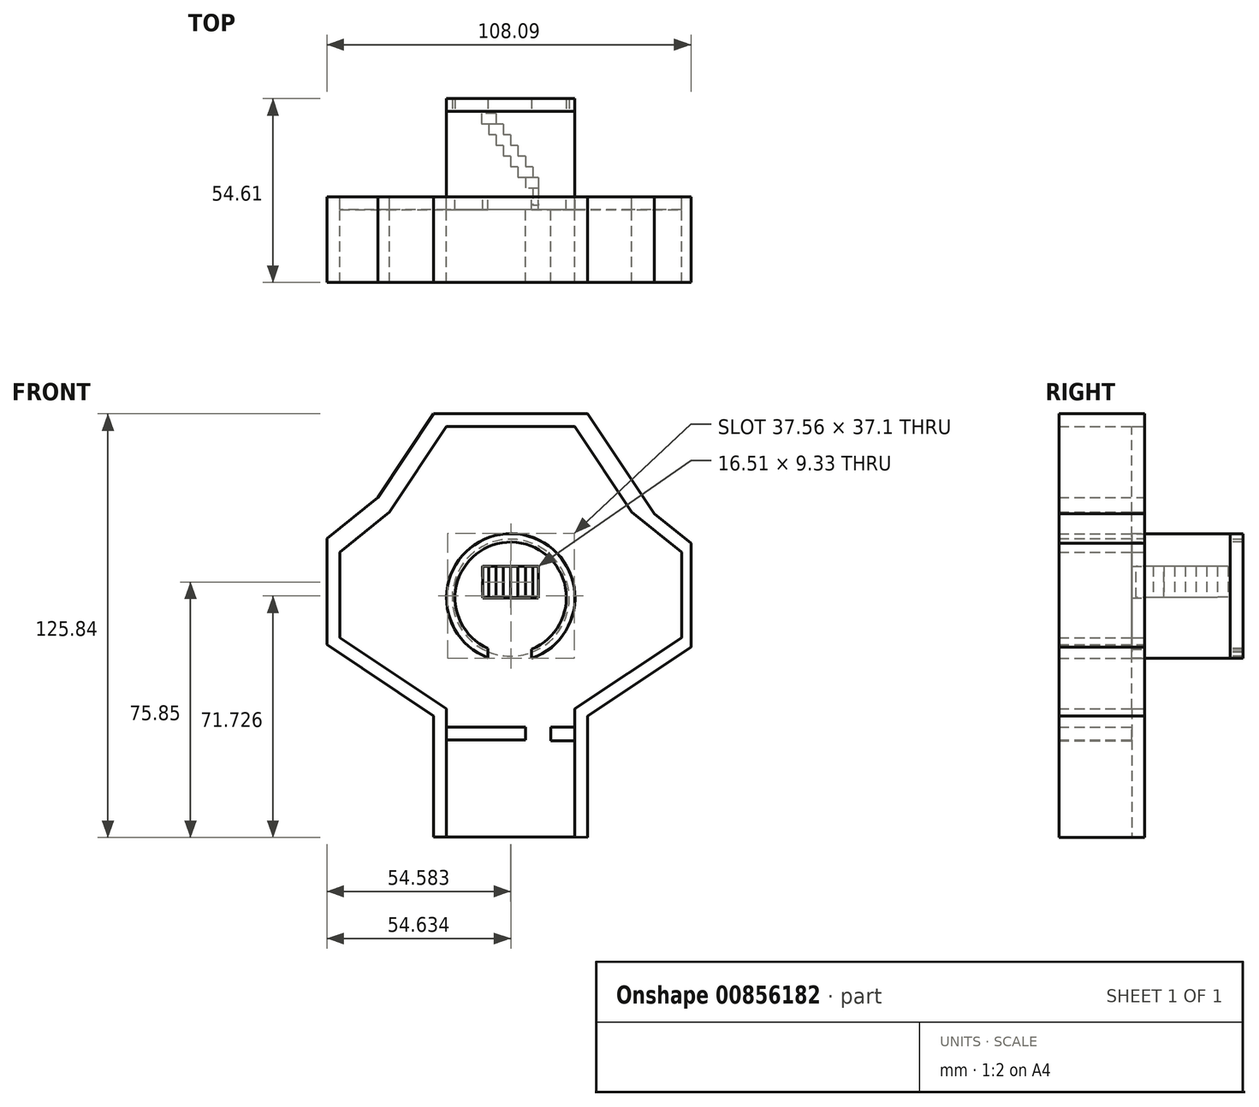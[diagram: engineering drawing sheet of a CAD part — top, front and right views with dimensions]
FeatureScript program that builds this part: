
annotation { "Feature Type Name" : "Feature", "Feature Type Description" : "" }
export const myFeature = defineFeature(function(context is Context, id is Id, definition is map)
    precondition{}
    {
        {
            var Q0;
            Q0=qCreatedBy(makeId("Front.planeOp"),FACE);
            var sketch = newSketch(context, id + "F0", { "sketchPlane" : qUnion([Q0])});
            skLineSegment(sketch, "E0.left", {"start": v(-51.03, 0) * mm, "end": v(-51.03, -38.1) * mm});
            skLineSegment(sketch, "E0.right", {"start": v(-12.93, 0) * mm, "end": v(-12.93, -38.1) * mm});
            skLineSegment(sketch, "E1", {"start": v(-12.93, 0) * mm, "end": v(18.8, 21.1) * mm});
            skLineSegment(sketch, "E2", {"start": v(18.8, 21.1) * mm, "end": v(18.8, 46.5) * mm});
            skLineSegment(sketch, "E3", {"start": v(18.8, 46.5) * mm, "end": v(3.96, 58.46) * mm});
            skLineSegment(sketch, "E4", {"start": v(3.96, 58.46) * mm, "end": v(-12.93, 83.84) * mm});
            skLineSegment(sketch, "E5", {"start": v(-12.93, 83.84) * mm, "end": v(-51.03, 83.84) * mm});
            skLineSegment(sketch, "E6", {"start": v(-82.75, 46.5) * mm, "end": v(-82.75, 21.1) * mm});
            skLineSegment(sketch, "E7", {"start": v(-82.75, 21.1) * mm, "end": v(-51.03, 0) * mm});
            skLineSegment(sketch, "E8", {"start": v(-51.03, 83.84) * mm, "end": v(-67.91, 58.46) * mm});
            skLineSegment(sketch, "E9", {"start": v(-67.91, 58.46) * mm, "end": v(-82.75, 46.5) * mm});
            skArc(sketch, "E10", {"start": v(-25.76, 14.99) * mm, "mid": v(-31.68, 52.04) * mm, "end": v(-38.74, 15.19) * mm});
            skLineSegment(sketch, "E11", {"start": v(-51.03, -9.44) * mm, "end": v(-27.63, -9.44) * mm});
            skLineSegment(sketch, "E12", {"start": v(-19.86, -9.44) * mm, "end": v(-12.93, -9.44) * mm});
            skArc(sketch, "E13", {"start": v(-25.76, 14.99) * mm, "mid": v(-31.68, 52.08) * mm, "end": v(-38.74, 15.19) * mm});
            skLineSegment(sketch, "E14", {"start": v(-51.03, 83.84) * mm, "end": v(-54.84, 87.65) * mm});
            skLineSegment(sketch, "E15", {"start": v(-54.84, 87.65) * mm, "end": v(-9.12, 87.65) * mm});
            skLineSegment(sketch, "E16", {"start": v(-9.12, 87.65) * mm, "end": v(-12.93, 83.84) * mm});
            skLineSegment(sketch, "E17", {"start": v(-9.12, 87.65) * mm, "end": v(10.62, 57.99) * mm});
            skLineSegment(sketch, "E18", {"start": v(10.62, 57.99) * mm, "end": v(3.96, 58.46) * mm});
            skLineSegment(sketch, "E19", {"start": v(10.03, 58.46) * mm, "end": v(10.62, 57.99) * mm});
            skLineSegment(sketch, "E20", {"start": v(10.03, 58.46) * mm, "end": v(21.53, 49.2) * mm});
            skLineSegment(sketch, "E21", {"start": v(21.53, 49.2) * mm, "end": v(18.8, 46.5) * mm});
            skLineSegment(sketch, "E22", {"start": v(21.53, 49.2) * mm, "end": v(21.53, 18.35) * mm});
            skLineSegment(sketch, "E23", {"start": v(21.53, 18.35) * mm, "end": v(18.8, 21.1) * mm});
            skLineSegment(sketch, "E24", {"start": v(21.53, 18.35) * mm, "end": v(-9.12, -2.04) * mm});
            skLineSegment(sketch, "E25", {"start": v(-9.12, -2.04) * mm, "end": v(-12.93, 0) * mm});
            skLineSegment(sketch, "E26", {"start": v(-9.12, -2.04) * mm, "end": v(-9.12, -38.19) * mm});
            skLineSegment(sketch, "E27", {"start": v(-9.12, -38.19) * mm, "end": v(-12.93, -38.1) * mm});
            skPoint(sketch, "E28.endSnap0", {"position": v(-59.47, 71.15) * mm});
            skLineSegment(sketch, "E29", {"start": v(-71.39, 62.77) * mm, "end": v(-67.91, 58.46) * mm});
            skLineSegment(sketch, "E30", {"start": v(-71.39, 62.77) * mm, "end": v(-86.56, 50.55) * mm});
            skLineSegment(sketch, "E31", {"start": v(-86.56, 50.55) * mm, "end": v(-82.75, 46.5) * mm});
            skLineSegment(sketch, "E32", {"start": v(-86.56, 50.55) * mm, "end": v(-86.56, 19.07) * mm});
            skLineSegment(sketch, "E33", {"start": v(-86.56, 19.07) * mm, "end": v(-82.75, 21.1) * mm});
            skLineSegment(sketch, "E34", {"start": v(-86.56, 19.07) * mm, "end": v(-54.84, -2.04) * mm});
            skLineSegment(sketch, "E35", {"start": v(-54.84, -2.04) * mm, "end": v(-51.03, 0) * mm});
            skLineSegment(sketch, "E36", {"start": v(-54.84, -2.04) * mm, "end": v(-54.84, -38.1) * mm});
            skLineSegment(sketch, "E37", {"start": v(-54.84, -38.1) * mm, "end": v(-51.03, -38.1) * mm});
            skPoint(sketch, "E38.start.orphan", {"position": v(-64.05, 71.15) * mm});
            skLineSegment(sketch, "E39", {"start": v(-71.39, 62.77) * mm, "end": v(-54.84, 87.65) * mm});
            skArc(sketch, "E40", {"start": v(-25.76, 17.72) * mm, "mid": v(-31.68, 49.52) * mm, "end": v(-38.74, 17.96) * mm});
            skLineSegment(sketch, "E41", {"start": v(-38.74, 15.19) * mm, "end": v(-38.74, 17.96) * mm});
            skLineSegment(sketch, "E42", {"start": v(-25.76, 14.99) * mm, "end": v(-25.76, 17.72) * mm});
            skLineSegment(sketch, "E43", {"start": v(-51.03, -38.1) * mm, "end": v(-12.93, -38.1) * mm});
            skLineSegment(sketch, "E44", {"start": v(-31.98, 33) * mm, "end": v(-40.23, 33) * mm});
            skLineSegment(sketch, "E45", {"start": v(-31.98, 33.02) * mm, "end": v(-23.72, 33.02) * mm});
            skPoint(sketch, "E46.oppositeSnap0", {"position": v(-23.72, 33.02) * mm});
            skLineSegment(sketch, "E46.bottom", {"start": v(-40.23, 33) * mm, "end": v(-23.72, 33) * mm});
            skLineSegment(sketch, "E46.top", {"start": v(-40.23, 42.33) * mm, "end": v(-23.72, 42.33) * mm});
            skLineSegment(sketch, "E46.left", {"start": v(-40.23, 33) * mm, "end": v(-40.23, 42.33) * mm});
            skLineSegment(sketch, "E46.right", {"start": v(-23.72, 33) * mm, "end": v(-23.72, 42.33) * mm});
            skPoint(sketch, "E47.orphan", {"position": v(-48.49, 33) * mm});
            skPoint(sketch, "E48.orphan", {"position": v(-15.47, 33.02) * mm});
            skSolve(sketch);
        }
        {
            var Q0;
            Q0=makeQuery(id+"F0.imprint","IMPRINT",FACE,{"disambiguationData":[TD([[makeQuery(id+"F0.imprint","IMPRINT",EDGE,{"derivedFrom":sQuery(id+"F0.wireOp",EDGE,"E8")}),-1.0]])]});
            var Q1;
            Q1=makeQuery(id+"F0.imprint","IMPRINT",FACE,{"disambiguationData":[TD([[makeQuery(id+"F0.imprint","IMPRINT",EDGE,{"derivedFrom":sQuery(id+"F0.wireOp",EDGE,"E9")}),-1.0]])]});
            var Q2;
            Q2=makeQuery(id+"F0.imprint","IMPRINT",FACE,{"disambiguationData":[TD([[makeQuery(id+"F0.imprint","IMPRINT",EDGE,{"derivedFrom":sQuery(id+"F0.wireOp",EDGE,"E6")}),-1.0]])]});
            var Q3;
            Q3=makeQuery(id+"F0.imprint","IMPRINT",FACE,{"disambiguationData":[TD([[makeQuery(id+"F0.imprint","IMPRINT",EDGE,{"derivedFrom":sQuery(id+"F0.wireOp",EDGE,"E7")}),-1.0]])]});
            var Q4;
            {var subQ0=sQuery(id+"F0.wireOp",EDGE,"E35");Q4=makeQuery(id+"F0.imprint","IMPRINT",FACE,{"disambiguationData":[TD([[makeQuery(id+"F0.imprint","IMPRINT",EDGE,{"derivedFrom":subQ0}),-1.0]])]});}
            var Q5;
            Q5=makeQuery(id+"F0.imprint","IMPRINT",FACE,{"disambiguationData":[TD([[makeQuery(id+"F0.imprint","IMPRINT",EDGE,{"derivedFrom":sQuery(id+"F0.wireOp",EDGE,"E5")}),-1.0]])]});
            var Q6;
            Q6=makeQuery(id+"F0.imprint","IMPRINT",FACE,{"disambiguationData":[TD([[makeQuery(id+"F0.imprint","IMPRINT",EDGE,{"derivedFrom":sQuery(id+"F0.wireOp",EDGE,"E4")}),-1.0]])]});
            var Q7;
            Q7=makeQuery(id+"F0.imprint","IMPRINT",FACE,{"disambiguationData":[TD([[makeQuery(id+"F0.imprint","IMPRINT",EDGE,{"derivedFrom":sQuery(id+"F0.wireOp",EDGE,"E3")}),-1.0]])]});
            var Q8;
            Q8=makeQuery(id+"F0.imprint","IMPRINT",FACE,{"disambiguationData":[TD([[makeQuery(id+"F0.imprint","IMPRINT",EDGE,{"derivedFrom":sQuery(id+"F0.wireOp",EDGE,"E2")}),-1.0]])]});
            var Q9;
            Q9=makeQuery(id+"F0.imprint","IMPRINT",FACE,{"disambiguationData":[TD([[makeQuery(id+"F0.imprint","IMPRINT",EDGE,{"derivedFrom":sQuery(id+"F0.wireOp",EDGE,"E1")}),-1.0]])]});
            var Q10;
            {var subQ0=sQuery(id+"F0.wireOp",EDGE,"E25");Q10=makeQuery(id+"F0.imprint","IMPRINT",FACE,{"disambiguationData":[TD([[makeQuery(id+"F0.imprint","IMPRINT",EDGE,{"derivedFrom":subQ0}),1.0]])]});}
            extrude(context, id + "F1", {"entities" : qUnion([Q0, Q1, Q2, Q3, Q4, Q5, Q6, Q7, Q8, Q9, Q10]), "depth" : 25.4 * mm, "offsetDistance" : 25.4 * mm});
        }
        {
            var Q0;
            Q0=makeQuery(id+"F0.imprint","IMPRINT",FACE,{"disambiguationData":[TD([[makeQuery(id+"F0.imprint","IMPRINT",EDGE,{"derivedFrom":sQuery(id+"F0.wireOp",EDGE,"E10")}),1.0]])]});
            extrude(context, id + "F2", {"entities" : qUnion([Q0]), "endBound" : BoundingType.SYMMETRIC, "depth" : 50.8 * mm, "offsetDistance" : 25.4 * mm});
        }
        {
            var Q0;
            {var subQ0=sQuery(id+"F0.wireOp",EDGE,"E1");Q0=makeQuery(id+"F0.imprint","IMPRINT",FACE,{"disambiguationData":[TD([[makeQuery(id+"F0.imprint","IMPRINT",EDGE,{"derivedFrom":subQ0}),1.0]])]});}
            extrude(context, id + "F3", {"entities" : qUnion([Q0]), "depth" : 3.8 * mm, "offsetDistance" : 25.4 * mm});
        }
        {
            var Q0;
            Q0=makeQuery(id+"F2.opExtrude","CAP_FACE",FACE,{"disambiguationData":[OSD([sQuery(id+"F0.wireOp",EDGE,"E10"),sQuery(id+"F0.wireOp",EDGE,"E40"),sQuery(id+"F0.wireOp",EDGE,"E41"),sQuery(id+"F0.wireOp",EDGE,"E42")])],"isStart":true});
            var sketch = newSketch(context, id + "F4", { "sketchPlane" : qUnion([Q0])});
            skCircle(sketch, "E49", {"center": v(31.98, 33.02) * mm, "radius": 17.36 * mm});
            skSolve(sketch);
        }
        {
            var Q0;
            Q0=makeQuery(id+"F3.opExtrude","CAP_FACE",FACE,{"disambiguationData":[OSD([sQuery(id+"F0.wireOp",EDGE,"E0.left"),sQuery(id+"F0.wireOp",EDGE,"E0.right"),sQuery(id+"F0.wireOp",EDGE,"E1"),sQuery(id+"F0.wireOp",EDGE,"E2"),sQuery(id+"F0.wireOp",EDGE,"E3"),sQuery(id+"F0.wireOp",EDGE,"E4"),sQuery(id+"F0.wireOp",EDGE,"E5"),sQuery(id+"F0.wireOp",EDGE,"E6"),sQuery(id+"F0.wireOp",EDGE,"E7"),sQuery(id+"F0.wireOp",EDGE,"E8"),sQuery(id+"F0.wireOp",EDGE,"E9"),sQuery(id+"F0.wireOp",EDGE,"E13"),sQuery(id+"F0.wireOp",EDGE,"E40"),sQuery(id+"F0.wireOp",EDGE,"E41"),sQuery(id+"F0.wireOp",EDGE,"E42"),sQuery(id+"F0.wireOp",EDGE,"E43"),sQuery(id+"F0.wireOp",EDGE,"E46.bottom"),sQuery(id+"F0.wireOp",EDGE,"E46.top"),sQuery(id+"F0.wireOp",EDGE,"E46.left"),sQuery(id+"F0.wireOp",EDGE,"E46.right")])],"isStart":false});
            var sketch = newSketch(context, id + "F5", { "sketchPlane" : qUnion([Q0])});
            skLineSegment(sketch, "E50", {"start": v(-27.53, -9.19) * mm, "end": v(-51.03, -9.19) * mm});
            skLineSegment(sketch, "E51", {"start": v(-51.03, -9.19) * mm, "end": v(-51.03, -5.38) * mm});
            skLineSegment(sketch, "E52", {"start": v(-27.53, -9.19) * mm, "end": v(-27.53, -5.38) * mm});
            skLineSegment(sketch, "E53", {"start": v(-27.53, -5.38) * mm, "end": v(-51.03, -5.38) * mm});
            skLineSegment(sketch, "E54", {"start": v(-20.05, -9.46) * mm, "end": v(-12.93, -9.46) * mm});
            skLineSegment(sketch, "E55", {"start": v(-12.93, -9.46) * mm, "end": v(-12.93, -5.38) * mm});
            skLineSegment(sketch, "E56", {"start": v(-12.93, -5.38) * mm, "end": v(-20.05, -5.38) * mm});
            skLineSegment(sketch, "E57", {"start": v(-20.05, -5.38) * mm, "end": v(-20.05, -9.46) * mm});
            skSolve(sketch);
        }
        {
            var Q0;
            Q0=makeQuery(id+"F5.imprint","IMPRINT",FACE,{"disambiguationData":[TD([[makeQuery(id+"F5.imprint","IMPRINT",EDGE,{"derivedFrom":sQuery(id+"F5.wireOp",EDGE,"E50")}),-1.0]])]});
            var Q1;
            Q1=makeQuery(id+"F5.imprint","IMPRINT",FACE,{"disambiguationData":[TD([[makeQuery(id+"F5.imprint","IMPRINT",EDGE,{"derivedFrom":sQuery(id+"F5.wireOp",EDGE,"E54")}),1.0]])]});
            extrude(context, id + "F6", {"entities" : qUnion([Q0, Q1]), "depth" : 21.59 * mm, "offsetDistance" : 25.4 * mm});
        }
        {
            var Q0;
            {var subQ10=sQuery(id+"F0.wireOp",EDGE,"E1");Q0=makeQuery(id+"F0.imprint","IMPRINT",FACE,{"disambiguationData":[TD([[makeQuery(id+"F0.imprint","IMPRINT",EDGE,{"derivedFrom":subQ10}),1.0]])]});}
            var sketch = newSketch(context, id + "F7", { "sketchPlane" : qUnion([Q0])});
            skLineSegment(sketch, "E58.bottom", {"start": v(-23.25, 42.44) * mm, "end": v(-27.6, 42.44) * mm});
            skLineSegment(sketch, "E58.top", {"start": v(-23.25, 33.04) * mm, "end": v(-27.6, 33.04) * mm});
            skLineSegment(sketch, "E58.left", {"start": v(-23.25, 42.44) * mm, "end": v(-23.25, 33.04) * mm});
            skPoint(sketch, "E58.right.start.orphan", {"position": v(-40.64, 42.44) * mm});
            skPoint(sketch, "E59.orphan", {"position": v(-40.64, 33.04) * mm});
            skLineSegment(sketch, "E60", {"start": v(-27.6, 33.04) * mm, "end": v(-27.6, 42.44) * mm});
            skPoint(sketch, "E61.start.orphan", {"position": v(-31.95, 42.44) * mm});
            skPoint(sketch, "E62.orphan", {"position": v(-31.95, 33.04) * mm});
            skLineSegment(sketch, "E63", {"start": v(-25.42, 42.44) * mm, "end": v(-25.42, 33.04) * mm});
            skLineSegment(sketch, "E64", {"start": v(-27.6, 42.44) * mm, "end": v(-31.95, 42.44) * mm});
            skLineSegment(sketch, "E65", {"start": v(-31.95, 33.04) * mm, "end": v(-31.95, 42.44) * mm});
            skLineSegment(sketch, "E66", {"start": v(-31.95, 33.04) * mm, "end": v(-27.6, 33.04) * mm});
            skLineSegment(sketch, "E67", {"start": v(-29.77, 33.04) * mm, "end": v(-29.77, 42.44) * mm});
            skLineSegment(sketch, "E68", {"start": v(-31.95, 42.44) * mm, "end": v(-40.64, 42.44) * mm});
            skLineSegment(sketch, "E69", {"start": v(-36.3, 42.44) * mm, "end": v(-36.3, 33.04) * mm});
            skLineSegment(sketch, "E70", {"start": v(-36.3, 33.04) * mm, "end": v(-31.95, 33.04) * mm});
            skLineSegment(sketch, "E71", {"start": v(-34.12, 33.04) * mm, "end": v(-34.12, 42.44) * mm});
            skLineSegment(sketch, "E72", {"start": v(-34.12, 42.44) * mm, "end": v(-40.64, 42.44) * mm});
            skLineSegment(sketch, "E73", {"start": v(-40.64, 33.04) * mm, "end": v(-36.3, 33.04) * mm});
            skLineSegment(sketch, "E74", {"start": v(-38.47, 33.04) * mm, "end": v(-38.47, 42.44) * mm});
            skLineSegment(sketch, "E75", {"start": v(-40.64, 33.04) * mm, "end": v(-40.64, 42.44) * mm});
            skSolve(sketch);
        }
        {
            var Q0;
            {var subQ0=sQuery(id+"F7.wireOp",EDGE,"E63");var subQ1=sQuery(id+"F7.wireOp",EDGE,"E58.top");var subQ2=makeQuery(id+"F7.imprint","INTERSECT",VERTEX,{"derivedFrom":[subQ1,subQ0]});Q0=makeQuery(id+"F7.imprint","IMPRINT",FACE,{"disambiguationData":[TD([[makeQuery(id+"F7.imprint","IMPRINT",EDGE,{"disambiguationData":[TD([[subQ2,1.0]])],"derivedFrom":subQ0}),1.0]])]});}
            extrude(context, id + "F8", {"entities" : qUnion([Q0]), "endBound" : BoundingType.SYMMETRIC, "oppositeDirection" : true, "depth" : 5.08 * mm, "offsetDistance" : 25.4 * mm});
        }
        {
            var Q0;
            Q0=makeQuery(id+"F8.opExtrude","CAP_FACE",FACE,{"disambiguationData":[OSD([sQuery(id+"F0.wireOp",EDGE,"E46.top"),sQuery(id+"F0.wireOp",EDGE,"E46.right"),sQuery(id+"F7.wireOp",EDGE,"E58.top"),sQuery(id+"F7.wireOp",EDGE,"E63")])],"isStart":false});
            var sketch = newSketch(context, id + "F9", { "sketchPlane" : qUnion([Q0])});
            skLineSegment(sketch, "E76.bottom", {"start": v(25.42, 42.33) * mm, "end": v(27.63, 42.33) * mm});
            skLineSegment(sketch, "E76.top", {"start": v(25.42, 33.04) * mm, "end": v(27.63, 33.04) * mm});
            skLineSegment(sketch, "E76.left", {"start": v(25.42, 42.33) * mm, "end": v(25.42, 33.04) * mm});
            skLineSegment(sketch, "E76.right", {"start": v(27.63, 42.33) * mm, "end": v(27.63, 33.04) * mm});
            skLineSegment(sketch, "E77.bottom", {"start": v(23.72, 42.33) * mm, "end": v(25.42, 42.33) * mm});
            skLineSegment(sketch, "E77.top", {"start": v(23.72, 33.04) * mm, "end": v(25.42, 33.04) * mm});
            skLineSegment(sketch, "E77.left", {"start": v(23.72, 42.33) * mm, "end": v(23.72, 33.04) * mm});
            skSolve(sketch);
        }
        {
            var Q0;
            Q0=makeQuery(id+"F9.imprint","IMPRINT",FACE,{"disambiguationData":[TD([[makeQuery(id+"F9.imprint","IMPRINT",EDGE,{"derivedFrom":sQuery(id+"F9.wireOp",EDGE,"E76.bottom")}),-1.0]])]});
            extrude(context, id + "F10", {"entities" : qUnion([Q0]), "depth" : 3.17 * mm, "offsetDistance" : 25.4 * mm});
        }
        {
            var Q0;
            Q0=makeQuery(id+"F8.opExtrude","CAP_FACE",FACE,{"disambiguationData":[OSD([sQuery(id+"F0.wireOp",EDGE,"E46.top"),sQuery(id+"F0.wireOp",EDGE,"E46.right"),sQuery(id+"F7.wireOp",EDGE,"E58.top"),sQuery(id+"F7.wireOp",EDGE,"E63")])],"isStart":false});
            extrude(context, id + "F11", {"entities" : qUnion([Q0]), "depth" : 3.17 * mm, "offsetDistance" : 25.4 * mm});
        }
        {
            var Q0;
            Q0=makeQuery(id+"F10.opExtrude","CAP_FACE",FACE,{"disambiguationData":[OSD([sQuery(id+"F9.wireOp",EDGE,"E76.bottom"),sQuery(id+"F9.wireOp",EDGE,"E76.top"),sQuery(id+"F9.wireOp",EDGE,"E76.right"),sQuery(id+"F9.wireOp",EDGE,"E76.left")])],"isStart":false});
            var sketch = newSketch(context, id + "F12", { "sketchPlane" : qUnion([Q0])});
            skLineSegment(sketch, "E78.bottom", {"start": v(25.42, 42.33) * mm, "end": v(29.84, 42.33) * mm});
            skLineSegment(sketch, "E78.top", {"start": v(25.42, 33.1) * mm, "end": v(29.84, 33.1) * mm});
            skLineSegment(sketch, "E78.left", {"start": v(25.42, 42.33) * mm, "end": v(25.42, 33.1) * mm});
            skLineSegment(sketch, "E78.right", {"start": v(29.84, 42.33) * mm, "end": v(29.84, 33.1) * mm});
            skSolve(sketch);
        }
        {
            var Q0;
            {var subQ3=sQuery(id+"F12.wireOp",EDGE,"E78.right");Q0=makeQuery(id+"F12.imprint","IMPRINT",FACE,{"disambiguationData":[TD([[makeQuery(id+"F12.imprint","IMPRINT",EDGE,{"derivedFrom":subQ3}),-1.0]])]});}
            var Q1;
            {var subQ0=sQuery(id+"F12.wireOp",EDGE,"E78.left");Q1=makeQuery(id+"F12.imprint","IMPRINT",FACE,{"disambiguationData":[TD([[makeQuery(id+"F12.imprint","IMPRINT",EDGE,{"derivedFrom":subQ0}),1.0]])]});}
            extrude(context, id + "F13", {"entities" : qUnion([Q0, Q1]), "operationType" : NewBodyOperationType.ADD, "depth" : 3.17 * mm, "offsetDistance" : 25.4 * mm});
        }
        {
            var Q0;
            Q0=makeQuery(id+"F13.opExtrude","CAP_FACE",FACE,{"disambiguationData":[OSD([sQuery(id+"F12.wireOp",EDGE,"E78.bottom"),sQuery(id+"F12.wireOp",EDGE,"E78.top"),sQuery(id+"F12.wireOp",EDGE,"E78.left"),sQuery(id+"F12.wireOp",EDGE,"E78.right")])],"isStart":false});
            var sketch = newSketch(context, id + "F14", { "sketchPlane" : qUnion([Q0])});
            skLineSegment(sketch, "E79.bottom", {"start": v(27.63, 42.33) * mm, "end": v(32.05, 42.33) * mm});
            skLineSegment(sketch, "E79.top", {"start": v(27.63, 33.1) * mm, "end": v(32.05, 33.1) * mm});
            skLineSegment(sketch, "E79.left", {"start": v(27.63, 42.33) * mm, "end": v(27.63, 33.1) * mm});
            skLineSegment(sketch, "E79.right", {"start": v(32.05, 42.33) * mm, "end": v(32.05, 33.1) * mm});
            skSolve(sketch);
        }
        {
            var Q0;
            {var subQ2=sQuery(id+"F14.wireOp",EDGE,"E79.left");Q0=makeQuery(id+"F14.imprint","IMPRINT",FACE,{"disambiguationData":[TD([[makeQuery(id+"F14.imprint","IMPRINT",EDGE,{"derivedFrom":subQ2}),1.0]])]});}
            var Q1;
            {var subQ2=sQuery(id+"F14.wireOp",EDGE,"E79.right");Q1=makeQuery(id+"F14.imprint","IMPRINT",FACE,{"disambiguationData":[TD([[makeQuery(id+"F14.imprint","IMPRINT",EDGE,{"derivedFrom":subQ2}),-1.0]])]});}
            extrude(context, id + "F15", {"entities" : qUnion([Q0, Q1]), "operationType" : NewBodyOperationType.ADD, "depth" : 3.17 * mm, "offsetDistance" : 25.4 * mm});
        }
        {
            var Q0;
            Q0=makeQuery(id+"F15.opExtrude","CAP_FACE",FACE,{"disambiguationData":[OSD([sQuery(id+"F14.wireOp",EDGE,"E79.bottom"),sQuery(id+"F14.wireOp",EDGE,"E79.top"),sQuery(id+"F14.wireOp",EDGE,"E79.left"),sQuery(id+"F14.wireOp",EDGE,"E79.right")])],"isStart":false});
            var sketch = newSketch(context, id + "F16", { "sketchPlane" : qUnion([Q0])});
            skLineSegment(sketch, "E80.bottom", {"start": v(29.84, 42.33) * mm, "end": v(34.2, 42.33) * mm});
            skLineSegment(sketch, "E80.top", {"start": v(29.84, 33.1) * mm, "end": v(34.2, 33.1) * mm});
            skLineSegment(sketch, "E80.left", {"start": v(29.84, 42.33) * mm, "end": v(29.84, 33.1) * mm});
            skLineSegment(sketch, "E80.right", {"start": v(34.2, 42.33) * mm, "end": v(34.2, 33.1) * mm});
            skSolve(sketch);
        }
        {
            var Q0;
            {var subQ2=sQuery(id+"F16.wireOp",EDGE,"E80.right");Q0=makeQuery(id+"F16.imprint","IMPRINT",FACE,{"disambiguationData":[TD([[makeQuery(id+"F16.imprint","IMPRINT",EDGE,{"derivedFrom":subQ2}),-1.0]])]});}
            var Q1;
            {var subQ2=sQuery(id+"F16.wireOp",EDGE,"E80.left");Q1=makeQuery(id+"F16.imprint","IMPRINT",FACE,{"disambiguationData":[TD([[makeQuery(id+"F16.imprint","IMPRINT",EDGE,{"derivedFrom":subQ2}),1.0]])]});}
            extrude(context, id + "F17", {"entities" : qUnion([Q0, Q1]), "operationType" : NewBodyOperationType.ADD, "depth" : 3.17 * mm, "offsetDistance" : 25.4 * mm});
        }
        {
            var Q0;
            Q0=makeQuery(id+"F17.opExtrude","CAP_FACE",FACE,{"disambiguationData":[OSD([sQuery(id+"F16.wireOp",EDGE,"E80.bottom"),sQuery(id+"F16.wireOp",EDGE,"E80.top"),sQuery(id+"F16.wireOp",EDGE,"E80.left"),sQuery(id+"F16.wireOp",EDGE,"E80.right")])],"isStart":false});
            var sketch = newSketch(context, id + "F18", { "sketchPlane" : qUnion([Q0])});
            skLineSegment(sketch, "E81.bottom", {"start": v(32.02, 42.33) * mm, "end": v(36.4, 42.33) * mm});
            skLineSegment(sketch, "E81.top", {"start": v(32.02, 33.1) * mm, "end": v(36.4, 33.1) * mm});
            skLineSegment(sketch, "E81.left", {"start": v(32.02, 42.33) * mm, "end": v(32.02, 33.1) * mm});
            skLineSegment(sketch, "E81.right", {"start": v(36.4, 42.33) * mm, "end": v(36.4, 33.1) * mm});
            skSolve(sketch);
        }
        {
            var Q0;
            {var subQ2=sQuery(id+"F18.wireOp",EDGE,"E81.left");Q0=makeQuery(id+"F18.imprint","IMPRINT",FACE,{"disambiguationData":[TD([[makeQuery(id+"F18.imprint","IMPRINT",EDGE,{"derivedFrom":subQ2}),1.0]])]});}
            var Q1;
            {var subQ2=sQuery(id+"F18.wireOp",EDGE,"E81.right");Q1=makeQuery(id+"F18.imprint","IMPRINT",FACE,{"disambiguationData":[TD([[makeQuery(id+"F18.imprint","IMPRINT",EDGE,{"derivedFrom":subQ2}),-1.0]])]});}
            extrude(context, id + "F19", {"entities" : qUnion([Q0, Q1]), "operationType" : NewBodyOperationType.ADD, "depth" : 3.17 * mm, "offsetDistance" : 25.4 * mm});
        }
        {
            var Q0;
            Q0=makeQuery(id+"F19.opExtrude","CAP_FACE",FACE,{"disambiguationData":[OSD([sQuery(id+"F18.wireOp",EDGE,"E81.bottom"),sQuery(id+"F18.wireOp",EDGE,"E81.top"),sQuery(id+"F18.wireOp",EDGE,"E81.left"),sQuery(id+"F18.wireOp",EDGE,"E81.right")])],"isStart":false});
            var sketch = newSketch(context, id + "F20", { "sketchPlane" : qUnion([Q0])});
            skLineSegment(sketch, "E82.bottom", {"start": v(34.2, 42.33) * mm, "end": v(38.53, 42.33) * mm});
            skLineSegment(sketch, "E82.top", {"start": v(34.2, 33.1) * mm, "end": v(38.53, 33.1) * mm});
            skLineSegment(sketch, "E82.left", {"start": v(34.2, 42.33) * mm, "end": v(34.2, 33.1) * mm});
            skLineSegment(sketch, "E82.right", {"start": v(38.53, 42.33) * mm, "end": v(38.53, 33.1) * mm});
            skSolve(sketch);
        }
        {
            var Q0;
            {var subQ2=sQuery(id+"F20.wireOp",EDGE,"E82.right");Q0=makeQuery(id+"F20.imprint","IMPRINT",FACE,{"disambiguationData":[TD([[makeQuery(id+"F20.imprint","IMPRINT",EDGE,{"derivedFrom":subQ2}),-1.0]])]});}
            var Q1;
            {var subQ2=sQuery(id+"F20.wireOp",EDGE,"E82.left");Q1=makeQuery(id+"F20.imprint","IMPRINT",FACE,{"disambiguationData":[TD([[makeQuery(id+"F20.imprint","IMPRINT",EDGE,{"derivedFrom":subQ2}),1.0]])]});}
            extrude(context, id + "F21", {"entities" : qUnion([Q0, Q1]), "operationType" : NewBodyOperationType.ADD, "depth" : 3.17 * mm, "offsetDistance" : 25.4 * mm});
        }
        {
            var Q0;
            Q0=makeQuery(id+"F21.opExtrude","CAP_FACE",FACE,{"disambiguationData":[OSD([sQuery(id+"F20.wireOp",EDGE,"E82.bottom"),sQuery(id+"F20.wireOp",EDGE,"E82.top"),sQuery(id+"F20.wireOp",EDGE,"E82.left"),sQuery(id+"F20.wireOp",EDGE,"E82.right")])],"isStart":false});
            var sketch = newSketch(context, id + "F22", { "sketchPlane" : qUnion([Q0])});
            skLineSegment(sketch, "E83.bottom", {"start": v(36.37, 42.33) * mm, "end": v(40.68, 42.33) * mm});
            skLineSegment(sketch, "E83.top", {"start": v(36.37, 33.16) * mm, "end": v(40.68, 33.16) * mm});
            skLineSegment(sketch, "E83.left", {"start": v(36.37, 42.33) * mm, "end": v(36.37, 33.16) * mm});
            skLineSegment(sketch, "E83.right", {"start": v(40.68, 42.33) * mm, "end": v(40.68, 33.16) * mm});
            skSolve(sketch);
        }
        {
            var Q0;
            {var subQ3=sQuery(id+"F22.wireOp",EDGE,"E83.left");Q0=makeQuery(id+"F22.imprint","IMPRINT",FACE,{"disambiguationData":[TD([[makeQuery(id+"F22.imprint","IMPRINT",EDGE,{"derivedFrom":subQ3}),1.0]])]});}
            var Q1;
            {var subQ3=sQuery(id+"F22.wireOp",EDGE,"E83.right");Q1=makeQuery(id+"F22.imprint","IMPRINT",FACE,{"disambiguationData":[TD([[makeQuery(id+"F22.imprint","IMPRINT",EDGE,{"derivedFrom":subQ3}),-1.0]])]});}
            extrude(context, id + "F23", {"entities" : qUnion([Q0, Q1]), "operationType" : NewBodyOperationType.ADD, "depth" : 3.17 * mm, "offsetDistance" : 25.4 * mm});
        }
        {
            var Q0;
            {var subQ5=makeQuery(id+"F2.opExtrude","CAP_EDGE",EDGE,{"disambiguationData":[OSD([sQuery(id+"F0.wireOp",EDGE,"E40")])],"isStart":true});Q0=makeQuery(id+"F4.imprint","IMPRINT",FACE,{"disambiguationData":[TD([[makeQuery(id+"F4.imprint","IMPRINT",EDGE,{"derivedFrom":subQ5}),-1.0]])]});}
            var Q1;
            {var subQ5=makeQuery(id+"F2.opExtrude","CAP_EDGE",EDGE,{"disambiguationData":[OSD([sQuery(id+"F0.wireOp",EDGE,"E10")])],"isStart":true});Q1=makeQuery(id+"F4.imprint","IMPRINT",FACE,{"disambiguationData":[TD([[makeQuery(id+"F4.imprint","IMPRINT",EDGE,{"derivedFrom":subQ5}),-1.0]])]});}
            extrude(context, id + "F24", {"entities" : qUnion([Q0, Q1]), "depth" : 3.8 * mm, "offsetDistance" : 25.4 * mm});
        }
    });
